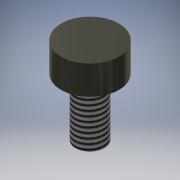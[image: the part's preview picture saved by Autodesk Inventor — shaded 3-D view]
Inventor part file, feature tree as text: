
AUTODESK INVENTOR PART (.ipt)
format: ipt  version: 2016 (Build 200138000, 138)  size: 120,320 bytes
history: native  units: mm
features: sketch x3, extrude x2, other x1, thread x1
ambient origin geometry x1: Origin
bodies: Body1 (feature_tree)
feature tree (7):
  other  "ソリッド1"
  extrude  "押し出し1"  Depth=3.0mm
  extrude  "押し出し2"  Depth=6.0mm TaperAngle=0.0deg
  thread  "ねじ1"
  sketch  "スケッチ4"
  sketch  "スケッチ1"
  sketch  "スケッチ2"
